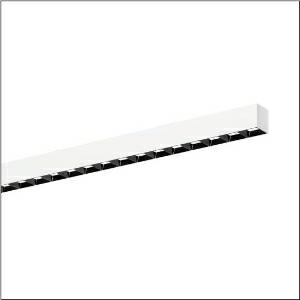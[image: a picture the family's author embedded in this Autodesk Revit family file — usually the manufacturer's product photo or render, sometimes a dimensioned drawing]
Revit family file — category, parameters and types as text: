
# Revit family: silica_r__21_51mx24dc4awb_a921
name_source: partatom
category: Lighting Fixtures
units: mm (PartAtom-declared; Revit-internal decimal feet)

## family parameters
Cut with Voids When Loaded = No
Host = Face
Light Source = No
Part Type = Normal
Room Calculation Point = No
Round Connector Dimension = Use Diameter
Shared = No

## types (1)
- --- (1 x LED, 10800 lm, 73.7 W, 4000K)
    Apparent Load = 74 VA
    CIE Flux Codes = 74 94 99 100 100
    Color Rendering = 80
    Color Temperature = 4000K
    Default Elevation = 1800 mm
    Description = Silica® 21, office luminaire, primary light control with darklight reflector, of PMMA, black, CAT 2 (L<= 3000cd/m²), light emission: direct distribution, primary light characteristic: asymmetric, installation type: surface-mounted, LED, rated luminous flux: 10.800lm, luminous efficacy: 147lm/W, light colour: 840, colour temperature: 4000K, control gear: DALI 2, with terminal, 3+2-pole, max. 2.5mm², mains connection: 220..240V, AC, 50/60Hz, rated input power: 73.7W, luminaire housing, of aluminium, traffic white (RAL 9016), length: 3.004mm, width: 53mm, height: 53mm, protection rating (complete): IP20, insulation class (complete): insulation class I (protective earthing), certification: CE, permissible operating ambient temperature: 0..+35°C, standard: EN 50419, packaging unit: 1 piece
    Height = 53 mm
    Lamp = 1 x LED
    Lamp Light Flux = 10800 lm
    Lamp Power = 73.7 W
    Lamp count = 1
    Length = 3004 mm
    Luminous efficacy = 147 lm/W
    Manufacturer = Siteco
    ModVariant = No
    Model = 51MX24DC4AWB
    Mounting Place = Ceiling
    Mounting Type = Surface mounted
    Number of Poles = 1
    OnlyDefault = Yes
    Power Factor = 1
    Product Name = Silica® 21
    Product group = office luminaire | ceiling mounted
    ProductGroupID = 302
    Protection Class = Protection class I
    Protection Degree = IP 20
    RLX_Detail_Level = 1
    RLX_Emergency_Light_Flux = 0 lm
    RLX_Emergency_Type = 0
    RLX_Emergency_Type_DB = No
    RlxData = <blob elided: 62757 chars, md5=bda12348>
    Socket = socket
    Standby Power = 0 W
    System Light Flux = 10800 lm
    System Power = 74 W
    Type Comments = factory setting: luminous flux: 100 % | dim-lin: 254 | 418 mA
    Type Image = l_1335873.jpg
    URL = http://relux.com
    VarID = @adj_123118
    Voltage = 0 V
    Weight = 0.00 kg
    Width = 53 mm

## geometry (parser evidence)
native form markers: Blend x4, Sweep x10
no freeform markers — native parametric forms only
